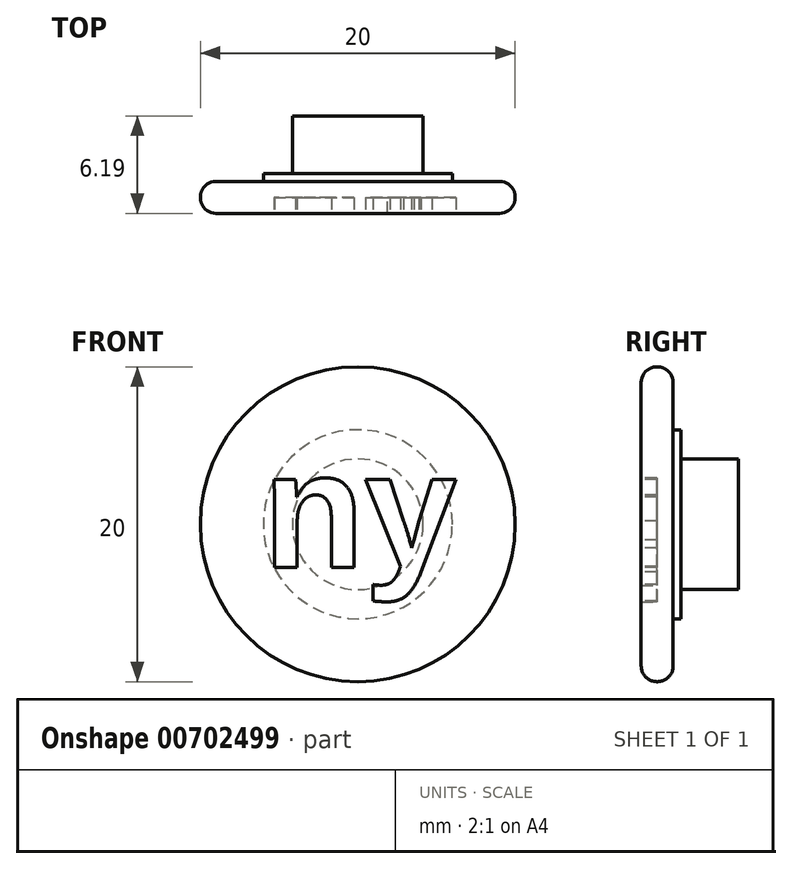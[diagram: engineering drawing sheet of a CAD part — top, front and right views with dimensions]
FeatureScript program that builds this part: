
annotation { "Feature Type Name" : "Feature", "Feature Type Description" : "" }
export const myFeature = defineFeature(function(context is Context, id is Id, definition is map)
    precondition{}
    {
        {
            var Q0;
            Q0=qCreatedBy(makeId("Front.planeOp"),FACE);
            var sketch = newSketch(context, id + "F0", { "sketchPlane" : qUnion([Q0])});
            skCircle(sketch, "E0", {"center": v(0, 0) * mm, "radius": 10 * mm});
            skCircle(sketch, "E1", {"center": v(0, 0) * mm, "radius": 6 * mm});
            skCircle(sketch, "E2", {"center": v(0, 0) * mm, "radius": 4.15 * mm});
            skSolve(sketch);
        }
        {
            var Q0;
            Q0=makeQuery(id+"F0.imprint","IMPRINT",FACE,{"disambiguationData":[TD([[makeQuery(id+"F0.imprint","IMPRINT",EDGE,{"derivedFrom":sQuery(id+"F0.wireOp",EDGE,"E0")}),1.0]])]});
            extrude(context, id + "F1", {"entities" : qUnion([Q0]), "oppositeDirection" : true, "depth" : 2.03 * mm, "offsetDistance" : 25 * mm});
        }
        {
            var Q0;
            Q0=makeQuery(id+"F0.imprint","IMPRINT",FACE,{"disambiguationData":[TD([[makeQuery(id+"F0.imprint","IMPRINT",EDGE,{"derivedFrom":sQuery(id+"F0.wireOp",EDGE,"E1")}),1.0]])]});
            var Q1;
            Q1 = qSketchRegion(id + "F5", true);
            extrude(context, id + "F2", {"entities" : qUnion([Q0, Q1]), "operationType" : NewBodyOperationType.ADD, "oppositeDirection" : true, "depth" : 2.52 * mm, "offsetDistance" : 25 * mm});
        }
        {
            var Q0;
            Q0=makeQuery(id+"F0.imprint","IMPRINT",FACE,{"disambiguationData":[TD([[makeQuery(id+"F0.imprint","IMPRINT",EDGE,{"derivedFrom":sQuery(id+"F0.wireOp",EDGE,"E2")}),1.0]])]});
            var Q1;
            Q1 = qSketchRegion(id + "F5", true);
            extrude(context, id + "F3", {"entities" : qUnion([Q0, Q1]), "operationType" : NewBodyOperationType.ADD, "oppositeDirection" : true, "depth" : 6.2 * mm, "offsetDistance" : 25 * mm});
        }
        {
            var Q0;
            Q0=makeQuery(id+"F1.opExtrude","SWEPT_FACE",FACE,{"disambiguationData":[OSD([sQuery(id+"F0.wireOp",EDGE,"E0")])]});
            fillet(context, id + "F4", {"entities" : qUnion([Q0]), "radius" : 1 * mm, "tangentPropagation" : true, "allowEdgeOverflow" : false});
        }
        {
            var Q0;
            Q0=qCreatedBy(makeId("Front.planeOp"),FACE);
            var sketch = newSketch(context, id + "F5", { "sketchPlane" : qUnion([Q0])});
            skText(sketch, "E3", { "text": "ny", "fontName": "Arimo-Bold.ttf"});
            const initialGuessF5  = {"E3": [-0.00603, -0.00274, 1, 0, 0.0076]};
            skSetInitialGuess(sketch, initialGuessF5);
            skSolve(sketch);
        }
        {
            var Q0;
            Q0 = qSketchRegion(id + "F5", true);
            extrude(context, id + "F6", {"entities" : qUnion([Q0]), "operationType" : NewBodyOperationType.REMOVE, "oppositeDirection" : true, "depth" : 1 * mm, "offsetDistance" : 25 * mm});
        }
    });
